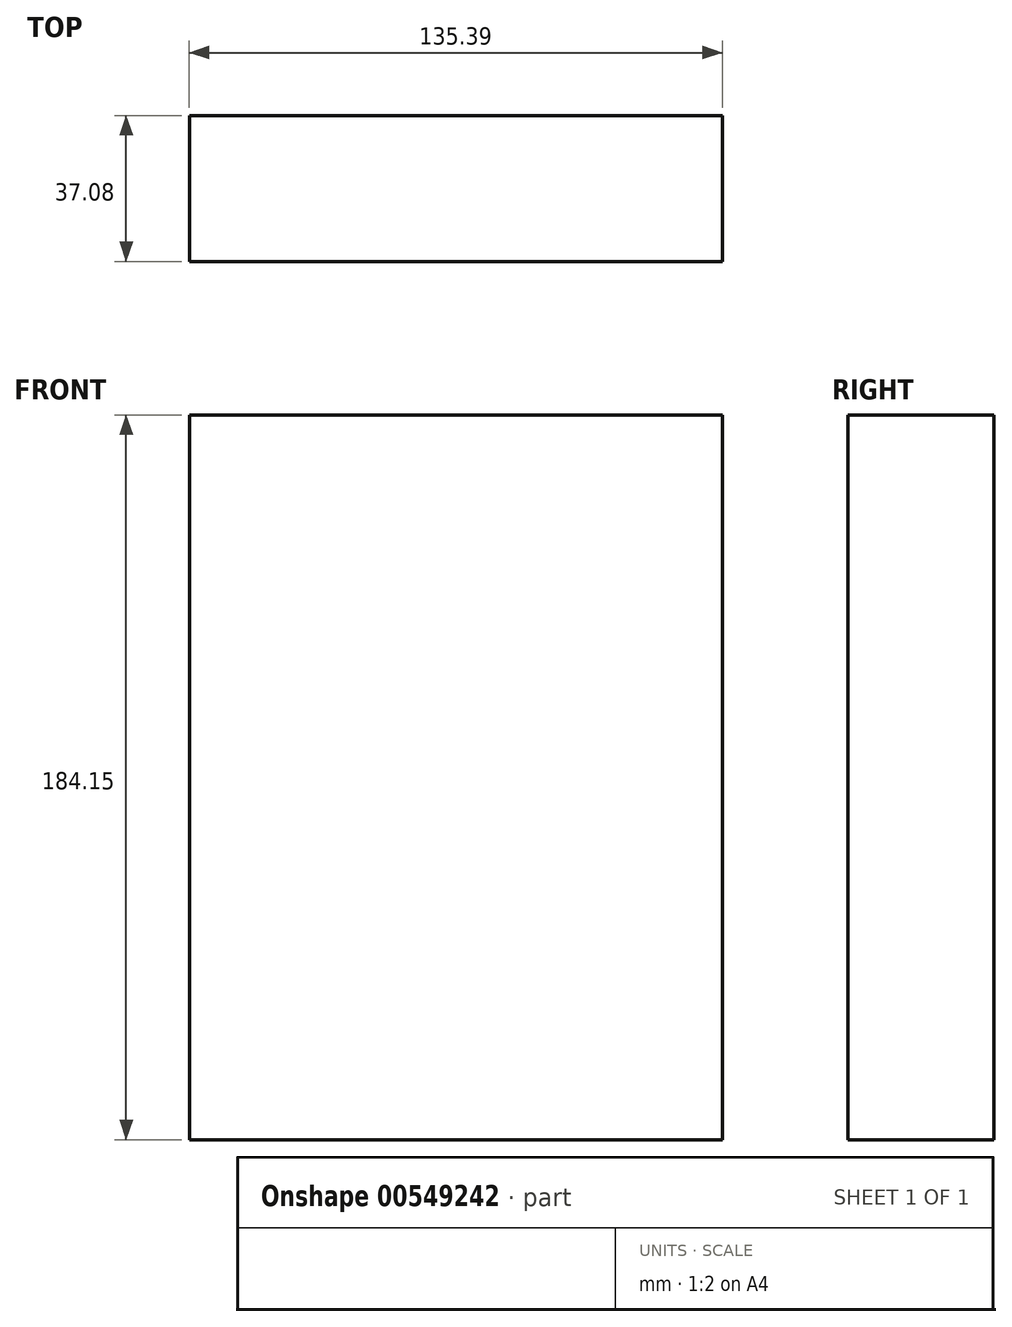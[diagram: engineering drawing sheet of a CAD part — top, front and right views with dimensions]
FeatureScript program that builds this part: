
annotation { "Feature Type Name" : "Feature", "Feature Type Description" : "" }
export const myFeature = defineFeature(function(context is Context, id is Id, definition is map)
    precondition{}
    {
        {
            var Q0;
            Q0=qCreatedBy(makeId("Front.planeOp"),FACE);
            var sketch = newSketch(context, id + "F0", { "sketchPlane" : qUnion([Q0])});
            skLineSegment(sketch, "E0.bottom", {"start": v(-30.84, 136.03) * mm, "end": v(104.55, 136.03) * mm});
            skLineSegment(sketch, "E0.top", {"start": v(-30.84, -48.12) * mm, "end": v(104.55, -48.12) * mm});
            skLineSegment(sketch, "E0.left", {"start": v(-30.84, 136.03) * mm, "end": v(-30.84, -48.12) * mm});
            skLineSegment(sketch, "E0.right", {"start": v(104.55, 136.03) * mm, "end": v(104.55, -48.12) * mm});
            skLineSegment(sketch, "E1.bottom", {"start": v(-30.84, 136.03) * mm, "end": v(0, 136.03) * mm});
            skLineSegment(sketch, "E1.top", {"start": v(-30.84, 105.2) * mm, "end": v(0, 105.2) * mm});
            skLineSegment(sketch, "E1.left", {"start": v(-30.84, 136.03) * mm, "end": v(-30.84, 105.2) * mm});
            skLineSegment(sketch, "E1.right", {"start": v(0, 136.03) * mm, "end": v(0, 105.2) * mm});
            skLineSegment(sketch, "E2.bottom", {"start": v(0, 105.2) * mm, "end": v(30.84, 105.2) * mm});
            skLineSegment(sketch, "E2.top", {"start": v(0, 136.03) * mm, "end": v(30.84, 136.03) * mm});
            skLineSegment(sketch, "E2.left", {"start": v(0, 105.2) * mm, "end": v(0, 136.03) * mm});
            skLineSegment(sketch, "E2.right", {"start": v(30.84, 105.2) * mm, "end": v(30.84, 136.03) * mm});
            skLineSegment(sketch, "E3.bottom", {"start": v(30.84, 105.2) * mm, "end": v(61.67, 105.2) * mm});
            skLineSegment(sketch, "E3.top", {"start": v(30.84, 136.03) * mm, "end": v(61.67, 136.03) * mm});
            skLineSegment(sketch, "E3.right", {"start": v(61.67, 105.2) * mm, "end": v(61.67, 136.03) * mm});
            skLineSegment(sketch, "E4.bottom", {"start": v(61.67, 105.2) * mm, "end": v(92.5, 105.2) * mm});
            skLineSegment(sketch, "E4.top", {"start": v(61.67, 136.03) * mm, "end": v(92.5, 136.03) * mm});
            skLineSegment(sketch, "E4.right", {"start": v(92.5, 105.2) * mm, "end": v(92.5, 136.03) * mm});
            skSolve(sketch);
        }
        {
            var Q0;
            Q0 = qSketchRegion(id + "F0", true);
            extrude(context, id + "F1", {"entities" : qUnion([Q0]), "depth" : 37.08 * mm, "offsetDistance" : 25.4 * mm});
        }
    });
